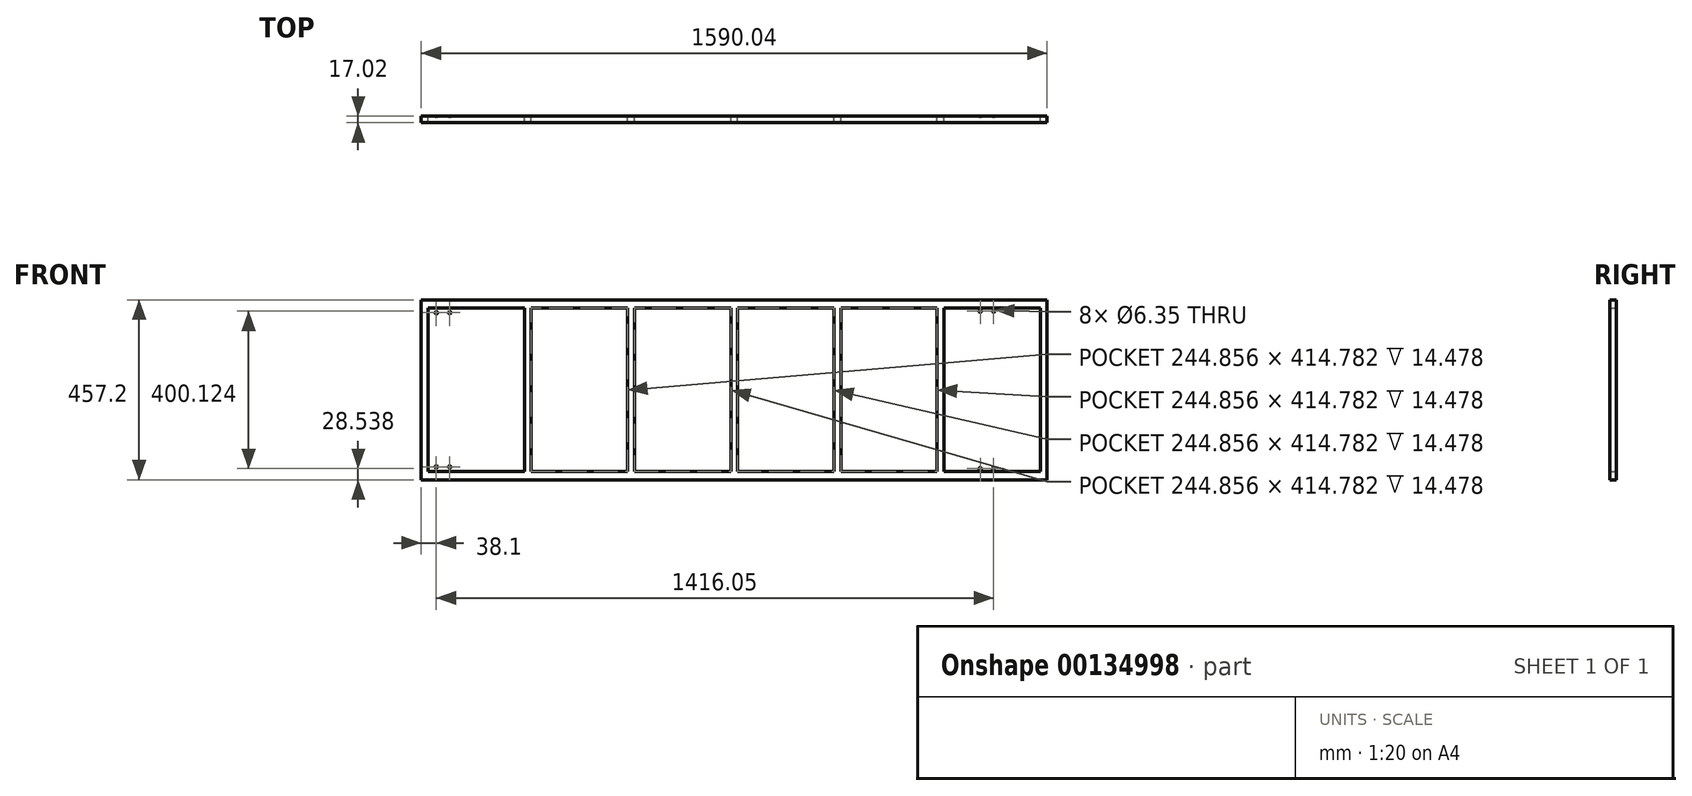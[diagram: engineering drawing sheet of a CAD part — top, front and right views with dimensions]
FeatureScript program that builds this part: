
annotation { "Feature Type Name" : "Feature", "Feature Type Description" : "" }
export const myFeature = defineFeature(function(context is Context, id is Id, definition is map)
    precondition{}
    {
        {
            var Q0;
            Q0=qCreatedBy(makeId("Front.planeOp"),FACE);
            var sketch = newSketch(context, id + "F0", { "sketchPlane" : qUnion([Q0])});
            skLineSegment(sketch, "E0.bottom", {"start": v(139.7, 228.6) * mm, "end": v(-139.7, 228.6) * mm});
            skLineSegment(sketch, "E0.top", {"start": v(139.7, -228.6) * mm, "end": v(-139.7, -228.6) * mm});
            skLineSegment(sketch, "E0.left", {"start": v(139.7, 207.4) * mm, "end": v(139.7, -207.4) * mm});
            skLineSegment(sketch, "E0.right", {"start": v(-139.7, 228.6) * mm, "end": v(-139.7, -228.6) * mm});
            skPoint(sketch, "E0.middle", {"position": v(0, 0) * mm});
            skLineSegment(sketch, "E1.1.0.0", {"start": v(384.81, 207.4) * mm, "end": v(384.81, -207.4) * mm});
            skLineSegment(sketch, "E1.1.0.1", {"start": v(384.81, -228.6) * mm, "end": v(105.41, -228.6) * mm});
            skLineSegment(sketch, "E1.1.0.2", {"start": v(384.8, 228.6) * mm, "end": v(105.4, 228.6) * mm});
            skLineSegment(sketch, "E1.2.0.1", {"start": v(629.92, -228.6) * mm, "end": v(350.52, -228.6) * mm});
            skLineSegment(sketch, "E1.2.0.2", {"start": v(629.92, 228.6) * mm, "end": v(350.52, 228.6) * mm});
            skLineSegment(sketch, "E1.3.0.1", {"start": v(875.03, -228.6) * mm, "end": v(595.63, -228.6) * mm});
            skLineSegment(sketch, "E1.3.0.2", {"start": v(875.03, 228.6) * mm, "end": v(595.63, 228.6) * mm});
            skLineSegment(sketch, "E1.4.0.1", {"start": v(1120.14, -228.6) * mm, "end": v(840.74, -228.6) * mm});
            skLineSegment(sketch, "E1.4.0.2", {"start": v(1120.14, 228.6) * mm, "end": v(840.74, 228.6) * mm});
            skLineSegment(sketch, "E1.5.0.1", {"start": v(1365.25, -228.6) * mm, "end": v(1085.85, -228.6) * mm});
            skLineSegment(sketch, "E1.5.0.2", {"start": v(1365.25, 228.6) * mm, "end": v(1085.85, 228.6) * mm});
            skLineSegment(sketch, "E1.direction1", {"start": v(139.7, -228.6) * mm, "end": v(384.81, -228.6) * mm, "construction": true});
            skLineSegment(sketch, "E2.bottom", {"start": v(122.43, 207.4) * mm, "end": v(-122.43, 207.4) * mm});
            skLineSegment(sketch, "E2.top", {"start": v(122.43, -207.4) * mm, "end": v(-122.43, -207.4) * mm});
            skLineSegment(sketch, "E2.left", {"start": v(122.43, 207.4) * mm, "end": v(122.43, -207.4) * mm});
            skLineSegment(sketch, "E2.right", {"start": v(-122.43, 207.4) * mm, "end": v(-122.43, -207.4) * mm});
            skLineSegment(sketch, "E3.1.0.0", {"start": v(384.56, 207.4) * mm, "end": v(384.56, -207.4) * mm});
            skLineSegment(sketch, "E3.1.0.1", {"start": v(384.56, 207.4) * mm, "end": v(139.7, 207.4) * mm});
            skLineSegment(sketch, "E3.1.0.2", {"start": v(384.56, -207.4) * mm, "end": v(139.7, -207.4) * mm});
            skLineSegment(sketch, "E3.2.0.0", {"start": v(646.68, 207.4) * mm, "end": v(646.68, -207.4) * mm});
            skLineSegment(sketch, "E3.2.0.1", {"start": v(646.68, 207.4) * mm, "end": v(384.8, 207.4) * mm});
            skLineSegment(sketch, "E3.2.0.2", {"start": v(646.68, -207.4) * mm, "end": v(401.83, -207.4) * mm});
            skLineSegment(sketch, "E3.2.0.3", {"start": v(401.83, 207.4) * mm, "end": v(401.83, -207.4) * mm});
            skLineSegment(sketch, "E3.3.0.0", {"start": v(908.81, 207.4) * mm, "end": v(908.81, -207.4) * mm});
            skLineSegment(sketch, "E3.3.0.1", {"start": v(908.81, 207.4) * mm, "end": v(663.96, 207.4) * mm});
            skLineSegment(sketch, "E3.3.0.2", {"start": v(908.81, -207.4) * mm, "end": v(663.96, -207.4) * mm});
            skLineSegment(sketch, "E3.3.0.3", {"start": v(663.96, 207.4) * mm, "end": v(663.96, -207.4) * mm});
            skLineSegment(sketch, "E3.4.0.0", {"start": v(1170.94, 207.4) * mm, "end": v(1170.94, -207.4) * mm});
            skLineSegment(sketch, "E3.4.0.1", {"start": v(1170.94, 207.4) * mm, "end": v(926.08, 207.4) * mm});
            skLineSegment(sketch, "E3.4.0.2", {"start": v(1170.94, -207.4) * mm, "end": v(926.08, -207.4) * mm});
            skLineSegment(sketch, "E3.4.0.3", {"start": v(926.08, 207.4) * mm, "end": v(926.08, -207.4) * mm});
            skLineSegment(sketch, "E3.5.0.0", {"start": v(1433.07, 207.4) * mm, "end": v(1433.07, -207.4) * mm});
            skLineSegment(sketch, "E3.5.0.1", {"start": v(1433.07, 207.4) * mm, "end": v(1188.21, 207.4) * mm});
            skLineSegment(sketch, "E3.5.0.2", {"start": v(1433.07, -207.4) * mm, "end": v(1188.21, -207.4) * mm});
            skLineSegment(sketch, "E3.5.0.3", {"start": v(1188.21, 207.4) * mm, "end": v(1188.21, -207.4) * mm});
            skLineSegment(sketch, "E3.direction1", {"start": v(139.7, -207.4) * mm, "end": v(384.56, -207.4) * mm, "construction": true});
            skLineSegment(sketch, "E4", {"start": v(1365.25, 228.6) * mm, "end": v(1450.34, 228.6) * mm});
            skLineSegment(sketch, "E5", {"start": v(1450.34, 228.6) * mm, "end": v(1450.34, -228.6) * mm});
            skLineSegment(sketch, "E6", {"start": v(1450.34, -228.6) * mm, "end": v(1365.25, -228.6) * mm});
            skPoint(sketch, "E7.orphan", {"position": v(139.7, -228.6) * mm});
            skPoint(sketch, "E8.orphan", {"position": v(139.7, 228.6) * mm});
            skLineSegment(sketch, "E9.trimOffspring", {"start": v(1170.94, 207.4) * mm, "end": v(1120.14, 207.4) * mm});
            skLineSegment(sketch, "E10.trimOffspring", {"start": v(908.81, 207.4) * mm, "end": v(875.03, 207.4) * mm});
            skLineSegment(sketch, "E11.trimOffspring", {"start": v(1170.94, -207.4) * mm, "end": v(1120.14, -207.4) * mm});
            skLineSegment(sketch, "E12.trimOffspring", {"start": v(908.81, -207.4) * mm, "end": v(875.03, -207.4) * mm});
            skLineSegment(sketch, "E13.trimOffspring", {"start": v(646.68, 207.4) * mm, "end": v(629.92, 207.4) * mm});
            skLineSegment(sketch, "E14.trimOffspring", {"start": v(646.68, -207.4) * mm, "end": v(629.92, -207.4) * mm});
            skSolve(sketch);
        }
        {
            var Q0;
            {var subQ20=sQuery(id+"F0.wireOp",EDGE,"E0.bottom");Q0=makeQuery(id+"F0.imprint","IMPRINT",FACE,{"disambiguationData":[TD([[makeQuery(id+"F0.imprint","IMPRINT",EDGE,{"derivedFrom":subQ20}),1.0]])]});}
            extrude(context, id + "F1", {"entities" : qUnion([Q0]), "depth" : 17.02 * mm});
        }
        {
            var Q0;
            Q0=makeQuery(id+"F0.imprint","IMPRINT",FACE,{"disambiguationData":[TD([[makeQuery(id+"F0.imprint","IMPRINT",EDGE,{"derivedFrom":sQuery(id+"F0.wireOp",EDGE,"E2.bottom")}),1.0]])]});
            var Q1;
            Q1=makeQuery(id+"F0.imprint","IMPRINT",FACE,{"disambiguationData":[TD([[makeQuery(id+"F0.imprint","IMPRINT",EDGE,{"derivedFrom":sQuery(id+"F0.wireOp",EDGE,"E0.left")}),1.0]])]});
            var Q2;
            Q2=makeQuery(id+"F0.imprint","IMPRINT",FACE,{"disambiguationData":[TD([[makeQuery(id+"F0.imprint","IMPRINT",EDGE,{"derivedFrom":sQuery(id+"F0.wireOp",EDGE,"E1.1.0.0")}),1.0]])]});
            var Q3;
            Q3=makeQuery(id+"F0.imprint","IMPRINT",FACE,{"disambiguationData":[TD([[makeQuery(id+"F0.imprint","IMPRINT",EDGE,{"derivedFrom":sQuery(id+"F0.wireOp",EDGE,"E1.2.0.0")}),1.0]])]});
            var Q4;
            Q4=makeQuery(id+"F0.imprint","IMPRINT",FACE,{"disambiguationData":[TD([[makeQuery(id+"F0.imprint","IMPRINT",EDGE,{"derivedFrom":sQuery(id+"F0.wireOp",EDGE,"E1.3.0.0")}),1.0]])]});
            var Q5;
            Q5=makeQuery(id+"F0.imprint","IMPRINT",FACE,{"disambiguationData":[TD([[makeQuery(id+"F0.imprint","IMPRINT",EDGE,{"derivedFrom":sQuery(id+"F0.wireOp",EDGE,"E1.4.0.0")}),1.0]])]});
            var Q6;
            Q6=makeQuery(id+"F0.imprint","IMPRINT",FACE,{"disambiguationData":[TD([[makeQuery(id+"F0.imprint","IMPRINT",EDGE,{"derivedFrom":sQuery(id+"F0.wireOp",EDGE,"E3.1.0.0")}),-1.0]])]});
            var Q7;
            {var subQ7=sQuery(id+"F0.wireOp",EDGE,"E3.2.0.0");Q7=makeQuery(id+"F0.imprint","IMPRINT",FACE,{"disambiguationData":[TD([[makeQuery(id+"F0.imprint","IMPRINT",EDGE,{"derivedFrom":subQ7}),-1.0]])]});}
            var Q8;
            {var subQ2=sQuery(id+"F0.wireOp",EDGE,"E3.3.0.0");Q8=makeQuery(id+"F0.imprint","IMPRINT",FACE,{"disambiguationData":[TD([[makeQuery(id+"F0.imprint","IMPRINT",EDGE,{"derivedFrom":subQ2}),-1.0]])]});}
            var Q9;
            {var subQ1=sQuery(id+"F0.wireOp",EDGE,"E3.4.0.0");Q9=makeQuery(id+"F0.imprint","IMPRINT",FACE,{"disambiguationData":[TD([[makeQuery(id+"F0.imprint","IMPRINT",EDGE,{"derivedFrom":subQ1}),-1.0]])]});}
            var Q10;
            {var subQ0=sQuery(id+"F0.wireOp",EDGE,"E3.5.0.0");Q10=makeQuery(id+"F0.imprint","IMPRINT",FACE,{"disambiguationData":[TD([[makeQuery(id+"F0.imprint","IMPRINT",EDGE,{"derivedFrom":subQ0}),-1.0]])]});}
            var Q11;
            {var subQ16=sQuery(id+"F0.wireOp",EDGE,"E1.1.0.0");Q11=makeQuery(id+"F0.imprint","IMPRINT",FACE,{"disambiguationData":[TD([[makeQuery(id+"F0.imprint","IMPRINT",EDGE,{"derivedFrom":subQ16}),-1.0]])]});}
            var Q12;
            {var subQ0=sQuery(id+"F0.wireOp",EDGE,"E3.2.0.0");Q12=makeQuery(id+"F0.imprint","IMPRINT",FACE,{"disambiguationData":[TD([[makeQuery(id+"F0.imprint","IMPRINT",EDGE,{"derivedFrom":subQ0}),1.0]])]});}
            var Q13;
            {var subQ0=sQuery(id+"F0.wireOp",EDGE,"E3.3.0.0");Q13=makeQuery(id+"F0.imprint","IMPRINT",FACE,{"disambiguationData":[TD([[makeQuery(id+"F0.imprint","IMPRINT",EDGE,{"derivedFrom":subQ0}),1.0]])]});}
            var Q14;
            {var subQ0=sQuery(id+"F0.wireOp",EDGE,"E3.4.0.0");Q14=makeQuery(id+"F0.imprint","IMPRINT",FACE,{"disambiguationData":[TD([[makeQuery(id+"F0.imprint","IMPRINT",EDGE,{"derivedFrom":subQ0}),1.0]])]});}
            extrude(context, id + "F2", {"entities" : qUnion([Q0, Q1, Q2, Q3, Q4, Q5, Q6, Q7, Q8, Q9, Q10, Q11, Q12, Q13, Q14]), "operationType" : NewBodyOperationType.ADD, "depth" : 2.54 * mm});
        }
        {
            var Q0;
            {var subQ0=sQuery(id+"F0.wireOp",EDGE,"E0.left");var subQ1=sQuery(id+"F0.wireOp",EDGE,"E2.right");var subQ2=sQuery(id+"F0.wireOp",EDGE,"E2.top");var subQ3=sQuery(id+"F0.wireOp",EDGE,"E2.bottom");var subQ4=sQuery(id+"F0.wireOp",EDGE,"E3.5.0.2");var subQ5=sQuery(id+"F0.wireOp",EDGE,"E3.5.0.1");var subQ6=sQuery(id+"F0.wireOp",EDGE,"E3.5.0.0");var subQ7=sQuery(id+"F0.wireOp",EDGE,"E1.4.0.0");var subQ8=sQuery(id+"F0.wireOp",EDGE,"E3.5.0.3");var subQ9=sQuery(id+"F0.wireOp",EDGE,"E3.4.0.2");var subQ10=sQuery(id+"F0.wireOp",EDGE,"E3.4.0.1");var subQ11=sQuery(id+"F0.wireOp",EDGE,"E1.3.0.0");var subQ12=sQuery(id+"F0.wireOp",EDGE,"E3.4.0.3");var subQ13=sQuery(id+"F0.wireOp",EDGE,"E3.3.0.2");var subQ14=sQuery(id+"F0.wireOp",EDGE,"E3.3.0.1");var subQ15=sQuery(id+"F0.wireOp",EDGE,"E1.2.0.0");var subQ16=sQuery(id+"F0.wireOp",EDGE,"E3.3.0.3");var subQ17=sQuery(id+"F0.wireOp",EDGE,"E3.2.0.2");var subQ18=sQuery(id+"F0.wireOp",EDGE,"E3.2.0.1");var subQ19=sQuery(id+"F0.wireOp",EDGE,"E1.1.0.0");var subQ20=sQuery(id+"F0.wireOp",EDGE,"E3.2.0.3");var subQ21=sQuery(id+"F0.wireOp",EDGE,"E3.1.0.2");var subQ22=sQuery(id+"F0.wireOp",EDGE,"E3.1.0.1");var subQ23=sQuery(id+"F0.wireOp",EDGE,"E0.left");Q0=makeQuery(id+"F2.boolean.opBoolean","MERGE",FACE,{"derivedFrom":[makeQuery(id+"F1.opExtrude","CAP_FACE",FACE,{"disambiguationData":[OSD([sQuery(id+"F0.wireOp",EDGE,"E0.bottom"),sQuery(id+"F0.wireOp",EDGE,"E0.top"),subQ23,sQuery(id+"F0.wireOp",EDGE,"E0.right"),subQ19,sQuery(id+"F0.wireOp",EDGE,"E1.1.0.1"),sQuery(id+"F0.wireOp",EDGE,"E1.1.0.2"),subQ15,sQuery(id+"F0.wireOp",EDGE,"E1.2.0.1"),sQuery(id+"F0.wireOp",EDGE,"E1.2.0.2"),subQ11,sQuery(id+"F0.wireOp",EDGE,"E1.3.0.1"),sQuery(id+"F0.wireOp",EDGE,"E1.3.0.2"),subQ7,sQuery(id+"F0.wireOp",EDGE,"E1.4.0.1"),sQuery(id+"F0.wireOp",EDGE,"E1.4.0.2"),sQuery(id+"F0.wireOp",EDGE,"E1.5.0.0"),sQuery(id+"F0.wireOp",EDGE,"E1.5.0.1"),sQuery(id+"F0.wireOp",EDGE,"E1.5.0.2"),subQ3,subQ2,subQ1,subQ22,subQ21,subQ0,subQ18,subQ17,subQ20,subQ14,subQ13,subQ16,subQ10,subQ9,subQ12,subQ6,subQ5,subQ4,subQ8])],"isStart":true}),makeQuery(id+"F2.opExtrude","CAP_FACE",FACE,{"disambiguationData":[OSD([subQ23,subQ22,subQ21,subQ20])],"isStart":true}),makeQuery(id+"F2.opExtrude","CAP_FACE",FACE,{"disambiguationData":[OSD([subQ19,subQ18,subQ17,subQ16])],"isStart":true}),makeQuery(id+"F2.opExtrude","CAP_FACE",FACE,{"disambiguationData":[OSD([subQ15,subQ14,subQ13,subQ12])],"isStart":true}),makeQuery(id+"F2.opExtrude","CAP_FACE",FACE,{"disambiguationData":[OSD([subQ11,subQ10,subQ9,subQ8])],"isStart":true}),makeQuery(id+"F2.opExtrude","CAP_FACE",FACE,{"disambiguationData":[OSD([subQ7,subQ6,subQ5,subQ4])],"isStart":true}),makeQuery(id+"F2.opExtrude","CAP_FACE",FACE,{"disambiguationData":[OSD([subQ3,subQ2,subQ1,subQ0])],"isStart":true})]});}
            var sketch = newSketch(context, id + "F3", { "sketchPlane" : qUnion([Q0])});
            skCircle(sketch, "E15", {"center": v(-1314.45, 200.06) * mm, "radius": 9.7 * mm});
            skCircle(sketch, "E16", {"center": v(-1280.32, 200.06) * mm, "radius": 10.5 * mm});
            skCircle(sketch, "E17", {"center": v(101.6, 195.93) * mm, "radius": 10.98 * mm});
            skCircle(sketch, "E18", {"center": v(67.46, 195.93) * mm, "radius": 13.2 * mm});
            skCircle(sketch, "E19.MirrorC", {"center": v(67.46, -195.93) * mm, "radius": 13.2 * mm});
            skCircle(sketch, "E20.MirrorC", {"center": v(101.6, -195.93) * mm, "radius": 10.98 * mm});
            skCircle(sketch, "E21.MirrorC", {"center": v(-1314.45, -200.06) * mm, "radius": 9.7 * mm});
            skCircle(sketch, "E22.MirrorC", {"center": v(-1280.32, -200.06) * mm, "radius": 10.5 * mm});
            skSolve(sketch);
        }
        {
            var Q0;
            Q0=sQuery(id+"F3.wireOp",VERTEX,"E15.center");
            var Q1;
            Q1=sQuery(id+"F3.wireOp",VERTEX,"E16.center");
            var Q2;
            Q2=sQuery(id+"F3.wireOp",VERTEX,"E18.center");
            var Q3;
            Q3=sQuery(id+"F3.wireOp",VERTEX,"E17.center");
            var Q4;
            Q4=sQuery(id+"F3.wireOp",VERTEX,"E21.MirrorC.center");
            var Q5;
            Q5=sQuery(id+"F3.wireOp",VERTEX,"E22.MirrorC.center");
            var Q6;
            Q6=sQuery(id+"F3.wireOp",VERTEX,"E19.MirrorC.center");
            var Q7;
            Q7=sQuery(id+"F3.wireOp",VERTEX,"E20.MirrorC.center");
            var Q8;
            Q8=makeQuery(id+"F1.opExtrude","SWEPT_BODY",BODY,{"disambiguationData":[OSD([sQuery(id+"F0.wireOp",EDGE,"E0.bottom"),sQuery(id+"F0.wireOp",EDGE,"E0.top"),sQuery(id+"F0.wireOp",EDGE,"E0.left"),sQuery(id+"F0.wireOp",EDGE,"E0.right"),sQuery(id+"F0.wireOp",EDGE,"E1.1.0.0"),sQuery(id+"F0.wireOp",EDGE,"E1.1.0.1"),sQuery(id+"F0.wireOp",EDGE,"E1.1.0.2"),sQuery(id+"F0.wireOp",EDGE,"E1.2.0.0"),sQuery(id+"F0.wireOp",EDGE,"E1.2.0.1"),sQuery(id+"F0.wireOp",EDGE,"E1.2.0.2"),sQuery(id+"F0.wireOp",EDGE,"E1.3.0.0"),sQuery(id+"F0.wireOp",EDGE,"E1.3.0.1"),sQuery(id+"F0.wireOp",EDGE,"E1.3.0.2"),sQuery(id+"F0.wireOp",EDGE,"E1.4.0.0"),sQuery(id+"F0.wireOp",EDGE,"E1.4.0.1"),sQuery(id+"F0.wireOp",EDGE,"E1.4.0.2"),sQuery(id+"F0.wireOp",EDGE,"E1.5.0.0"),sQuery(id+"F0.wireOp",EDGE,"E1.5.0.1"),sQuery(id+"F0.wireOp",EDGE,"E1.5.0.2"),sQuery(id+"F0.wireOp",EDGE,"E2.bottom"),sQuery(id+"F0.wireOp",EDGE,"E2.top"),sQuery(id+"F0.wireOp",EDGE,"E2.right"),sQuery(id+"F0.wireOp",EDGE,"E3.1.0.1"),sQuery(id+"F0.wireOp",EDGE,"E3.1.0.2"),sQuery(id+"F0.wireOp",EDGE,"E0.left"),sQuery(id+"F0.wireOp",EDGE,"E3.2.0.1"),sQuery(id+"F0.wireOp",EDGE,"E3.2.0.2"),sQuery(id+"F0.wireOp",EDGE,"E3.2.0.3"),sQuery(id+"F0.wireOp",EDGE,"E3.3.0.1"),sQuery(id+"F0.wireOp",EDGE,"E3.3.0.2"),sQuery(id+"F0.wireOp",EDGE,"E3.3.0.3"),sQuery(id+"F0.wireOp",EDGE,"E3.4.0.1"),sQuery(id+"F0.wireOp",EDGE,"E3.4.0.2"),sQuery(id+"F0.wireOp",EDGE,"E3.4.0.3"),sQuery(id+"F0.wireOp",EDGE,"E3.5.0.0"),sQuery(id+"F0.wireOp",EDGE,"E3.5.0.1"),sQuery(id+"F0.wireOp",EDGE,"E3.5.0.2"),sQuery(id+"F0.wireOp",EDGE,"E3.5.0.3")])]});
            hole(context, id + "F4", {"style" : HoleStyle.SIMPLE, "endStyle" : HoleEndStyle.BLIND, "holeDiameter" : 6.35 * mm, "holeDepth" : 2.54 * mm, "locations" : qUnion([Q0, Q1, Q2, Q3, Q4, Q5, Q6, Q7]), "scope" : qUnion([Q8])});
        }
    });
